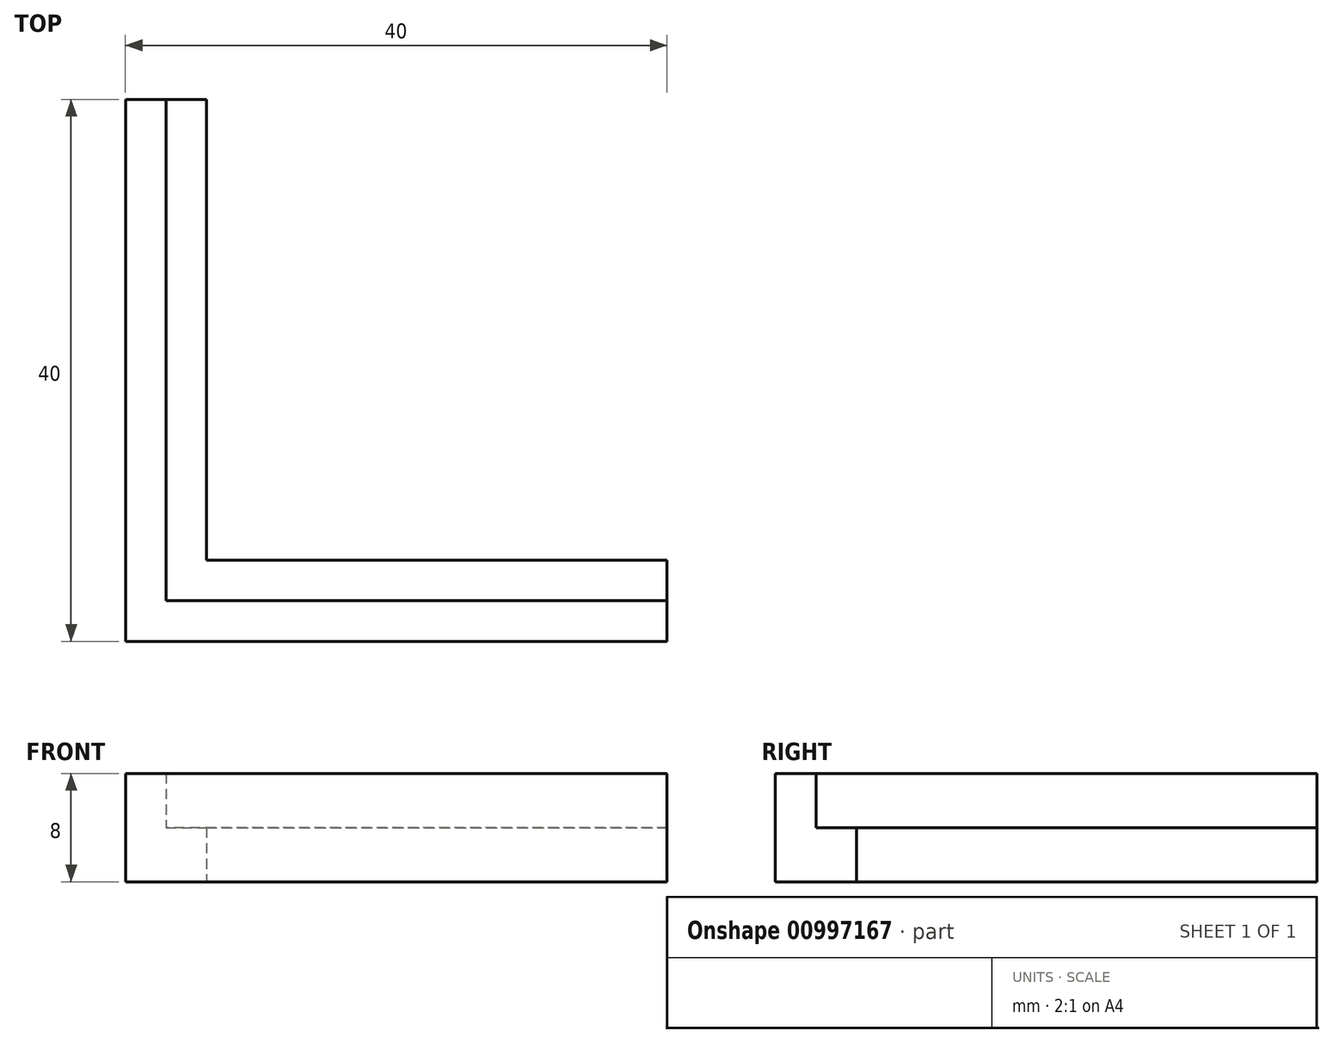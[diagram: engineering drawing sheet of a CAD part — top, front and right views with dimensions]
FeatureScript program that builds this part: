
annotation { "Feature Type Name" : "Feature", "Feature Type Description" : "" }
export const myFeature = defineFeature(function(context is Context, id is Id, definition is map)
    precondition{}
    {
        {
            var Q0;
            Q0=qCreatedBy(makeId("Top.planeOp"),FACE);
            var sketch = newSketch(context, id + "F0", { "sketchPlane" : qUnion([Q0])});
            skLineSegment(sketch, "E0.bottom", {"start": v(-15.62, 8.79) * mm, "end": v(35.18, 8.79) * mm, "construction": true});
            skLineSegment(sketch, "E0.top", {"start": v(-15.62, -42.01) * mm, "end": v(35.18, -42.01) * mm, "construction": true});
            skLineSegment(sketch, "E0.left", {"start": v(-15.62, 8.79) * mm, "end": v(-15.62, -42.01) * mm, "construction": true});
            skLineSegment(sketch, "E0.right", {"start": v(35.18, 8.79) * mm, "end": v(35.18, -42.01) * mm, "construction": true});
            skLineSegment(sketch, "E1", {"start": v(-2.92, 8.79) * mm, "end": v(-2.92, -3.91) * mm, "construction": true});
            skLineSegment(sketch, "E2", {"start": v(22.48, 8.79) * mm, "end": v(22.48, -3.91) * mm, "construction": true});
            skLineSegment(sketch, "E3", {"start": v(35.18, -29.31) * mm, "end": v(22.48, -29.31) * mm, "construction": true});
            skLineSegment(sketch, "E4", {"start": v(35.18, -3.91) * mm, "end": v(22.48, -3.91) * mm, "construction": true});
            skLineSegment(sketch, "E5", {"start": v(-2.92, -3.91) * mm, "end": v(-2.92, -29.31) * mm, "construction": true});
            skLineSegment(sketch, "E6", {"start": v(-2.92, -3.91) * mm, "end": v(-15.62, -3.91) * mm, "construction": true});
            skLineSegment(sketch, "E7", {"start": v(22.48, -3.91) * mm, "end": v(-2.92, -3.91) * mm, "construction": true});
            skLineSegment(sketch, "E8", {"start": v(22.48, -3.91) * mm, "end": v(22.48, -29.31) * mm, "construction": true});
            skLineSegment(sketch, "E9", {"start": v(22.48, -29.31) * mm, "end": v(-2.92, -29.31) * mm, "construction": true});
            skLineSegment(sketch, "E10", {"start": v(22.48, -29.31) * mm, "end": v(22.48, -42.01) * mm, "construction": true});
            skLineSegment(sketch, "E11", {"start": v(-2.92, -29.31) * mm, "end": v(-2.92, -42.01) * mm, "construction": true});
            skLineSegment(sketch, "E12", {"start": v(-2.92, -29.31) * mm, "end": v(-15.62, -29.31) * mm, "construction": true});
            skLineSegment(sketch, "E13", {"start": v(-12.12, 8.79) * mm, "end": v(-12.12, 5.29) * mm, "construction": true});
            skLineSegment(sketch, "E14", {"start": v(-15.62, -38.51) * mm, "end": v(-12.12, -38.51) * mm, "construction": true});
            skLineSegment(sketch, "E15", {"start": v(31.68, -42.01) * mm, "end": v(31.68, -38.51) * mm, "construction": true});
            skLineSegment(sketch, "E16", {"start": v(35.18, 5.29) * mm, "end": v(-12.12, 5.29) * mm, "construction": true});
            skLineSegment(sketch, "E17", {"start": v(-12.12, 5.29) * mm, "end": v(-12.12, -38.51) * mm, "construction": true});
            skLineSegment(sketch, "E18", {"start": v(-12.12, 5.29) * mm, "end": v(-15.62, 5.29) * mm, "construction": true});
            skLineSegment(sketch, "E19", {"start": v(-12.12, -38.51) * mm, "end": v(-12.12, -42.01) * mm, "construction": true});
            skLineSegment(sketch, "E20", {"start": v(-12.12, -38.51) * mm, "end": v(31.68, -38.51) * mm, "construction": true});
            skLineSegment(sketch, "E21", {"start": v(31.68, -38.51) * mm, "end": v(35.18, -38.51) * mm, "construction": true});
            skLineSegment(sketch, "E22", {"start": v(31.68, -38.51) * mm, "end": v(31.68, 5.29) * mm, "construction": true});
            skLineSegment(sketch, "E23", {"start": v(31.68, 5.29) * mm, "end": v(31.68, 8.79) * mm, "construction": true});
            skLineSegment(sketch, "E24", {"start": v(31.68, 5.29) * mm, "end": v(31.68, 5.29) * mm});
            skCircle(sketch, "E25", {"center": v(-2.92, 5.29) * mm, "radius": 3 * mm, "construction": true});
            skCircle(sketch, "E26", {"center": v(22.48, 5.29) * mm, "radius": 3 * mm, "construction": true});
            skCircle(sketch, "E27", {"center": v(31.68, -3.91) * mm, "radius": 3 * mm, "construction": true});
            skCircle(sketch, "E28", {"center": v(31.68, -29.31) * mm, "radius": 3 * mm, "construction": true});
            skCircle(sketch, "E29", {"center": v(22.48, -38.51) * mm, "radius": 3 * mm, "construction": true});
            skCircle(sketch, "E30", {"center": v(-2.92, -38.51) * mm, "radius": 3 * mm, "construction": true});
            skCircle(sketch, "E31", {"center": v(-12.12, -29.31) * mm, "radius": 3 * mm, "construction": true});
            skCircle(sketch, "E32", {"center": v(-12.12, -3.91) * mm, "radius": 3 * mm, "construction": true});
            skSolve(sketch);
        }
        {
            var Q0;
            Q0=qCreatedBy(makeId("Top.planeOp"),FACE);
            var sketch = newSketch(context, id + "F1", { "sketchPlane" : qUnion([Q0])});
            skLineSegment(sketch, "E33.bottom", {"start": v(-21.12, 14.29) * mm, "end": v(40.68, 14.29) * mm, "construction": true});
            skLineSegment(sketch, "E33.top", {"start": v(-21.12, -47.51) * mm, "end": v(40.68, -47.51) * mm});
            skLineSegment(sketch, "E33.left", {"start": v(-21.12, 14.29) * mm, "end": v(-21.12, -47.51) * mm});
            skLineSegment(sketch, "E33.right", {"start": v(40.68, 14.29) * mm, "end": v(40.68, -47.51) * mm, "construction": true});
            skLineSegment(sketch, "E34.bottom", {"start": v(-40.22, 33.39) * mm, "end": v(59.78, 33.39) * mm, "construction": true});
            skLineSegment(sketch, "E34.top", {"start": v(-40.22, -66.61) * mm, "end": v(59.78, -66.61) * mm});
            skLineSegment(sketch, "E34.left", {"start": v(-40.22, 33.39) * mm, "end": v(-40.22, -66.61) * mm});
            skLineSegment(sketch, "E34.right", {"start": v(59.78, 33.39) * mm, "end": v(59.78, -66.61) * mm, "construction": true});
            skLineSegment(sketch, "E35", {"start": v(-40.22, 33.39) * mm, "end": v(-21.12, 14.29) * mm});
            skLineSegment(sketch, "E36", {"start": v(40.68, -47.51) * mm, "end": v(59.78, -66.61) * mm});
            skLineSegment(sketch, "E37", {"start": v(-21.12, -47.51) * mm, "end": v(-40.22, -66.61) * mm, "construction": true});
            skSolve(sketch);
        }
        {
            var Q0;
            Q0=qSketchRegion(id+"F1",true);
            extrude(context, id + "F2", {"entities" : qUnion([Q0]), "depth" : 4 * mm, "offsetDistance" : 25 * mm});
        }
        {
            var Q0;
            Q0=makeQuery(id+"F2.opExtrude","CAP_FACE",FACE,{"disambiguationData":[OSD([sQuery(id+"F1.wireOp",EDGE,"E33.top"),sQuery(id+"F1.wireOp",EDGE,"E33.left"),sQuery(id+"F1.wireOp",EDGE,"E34.top"),sQuery(id+"F1.wireOp",EDGE,"E34.left"),sQuery(id+"F1.wireOp",EDGE,"E35"),sQuery(id+"F1.wireOp",EDGE,"E36")])],"isStart":false});
            var sketch = newSketch(context, id + "F3", { "sketchPlane" : qUnion([Q0])});
            skLineSegment(sketch, "E38", {"start": v(-40.22, -3.09) * mm, "end": v(-40.22, -66.61) * mm});
            skLineSegment(sketch, "E39", {"start": v(-40.22, -66.61) * mm, "end": v(15.73, -66.61) * mm});
            skLineSegment(sketch, "E40", {"start": v(15.73, -66.61) * mm, "end": v(15.73, -50.51) * mm});
            skLineSegment(sketch, "E41", {"start": v(15.73, -50.51) * mm, "end": v(-24.12, -50.51) * mm});
            skLineSegment(sketch, "E42", {"start": v(-24.12, -50.51) * mm, "end": v(-24.12, -3.09) * mm});
            skLineSegment(sketch, "E43", {"start": v(-24.12, -3.09) * mm, "end": v(-40.22, -3.09) * mm});
            skSolve(sketch);
        }
        {
            var Q0;
            Q0 = qSketchRegion(id + "F3", true);
            extrude(context, id + "F4", {"entities" : qUnion([Q0]), "operationType" : NewBodyOperationType.ADD, "depth" : 4 * mm, "offsetDistance" : 25 * mm});
        }
        {
            var Q0;
            Q0=qCreatedBy(makeId("Top.planeOp"),FACE);
            var sketch = newSketch(context, id + "F5", { "sketchPlane" : qUnion([Q0])});
            skLineSegment(sketch, "E44.bottom", {"start": v(12.88, -13.51) * mm, "end": v(-27.12, -13.51) * mm});
            skLineSegment(sketch, "E44.top", {"start": v(12.88, -53.51) * mm, "end": v(-27.12, -53.51) * mm});
            skLineSegment(sketch, "E44.left", {"start": v(12.88, -13.51) * mm, "end": v(12.88, -53.51) * mm});
            skLineSegment(sketch, "E44.right", {"start": v(-27.12, -13.51) * mm, "end": v(-27.12, -53.51) * mm});
            skLineSegment(sketch, "E45.bottom", {"start": v(-56.3, 39.62) * mm, "end": v(73.62, 39.62) * mm});
            skLineSegment(sketch, "E45.top", {"start": v(-56.3, -80.29) * mm, "end": v(73.62, -80.29) * mm});
            skLineSegment(sketch, "E45.left", {"start": v(-56.3, 39.62) * mm, "end": v(-56.3, -80.29) * mm});
            skLineSegment(sketch, "E45.right", {"start": v(73.62, 39.62) * mm, "end": v(73.62, -80.29) * mm});
            skSolve(sketch);
        }
        {
            var Q0;
            Q0 = qSketchRegion(id + "F5", true);
            extrude(context, id + "F6", {"entities" : qUnion([Q0]), "operationType" : NewBodyOperationType.REMOVE, "endBound" : BoundingType.THROUGH_ALL, "depth" : 25 * mm, "offsetDistance" : 25 * mm});
        }
    });
